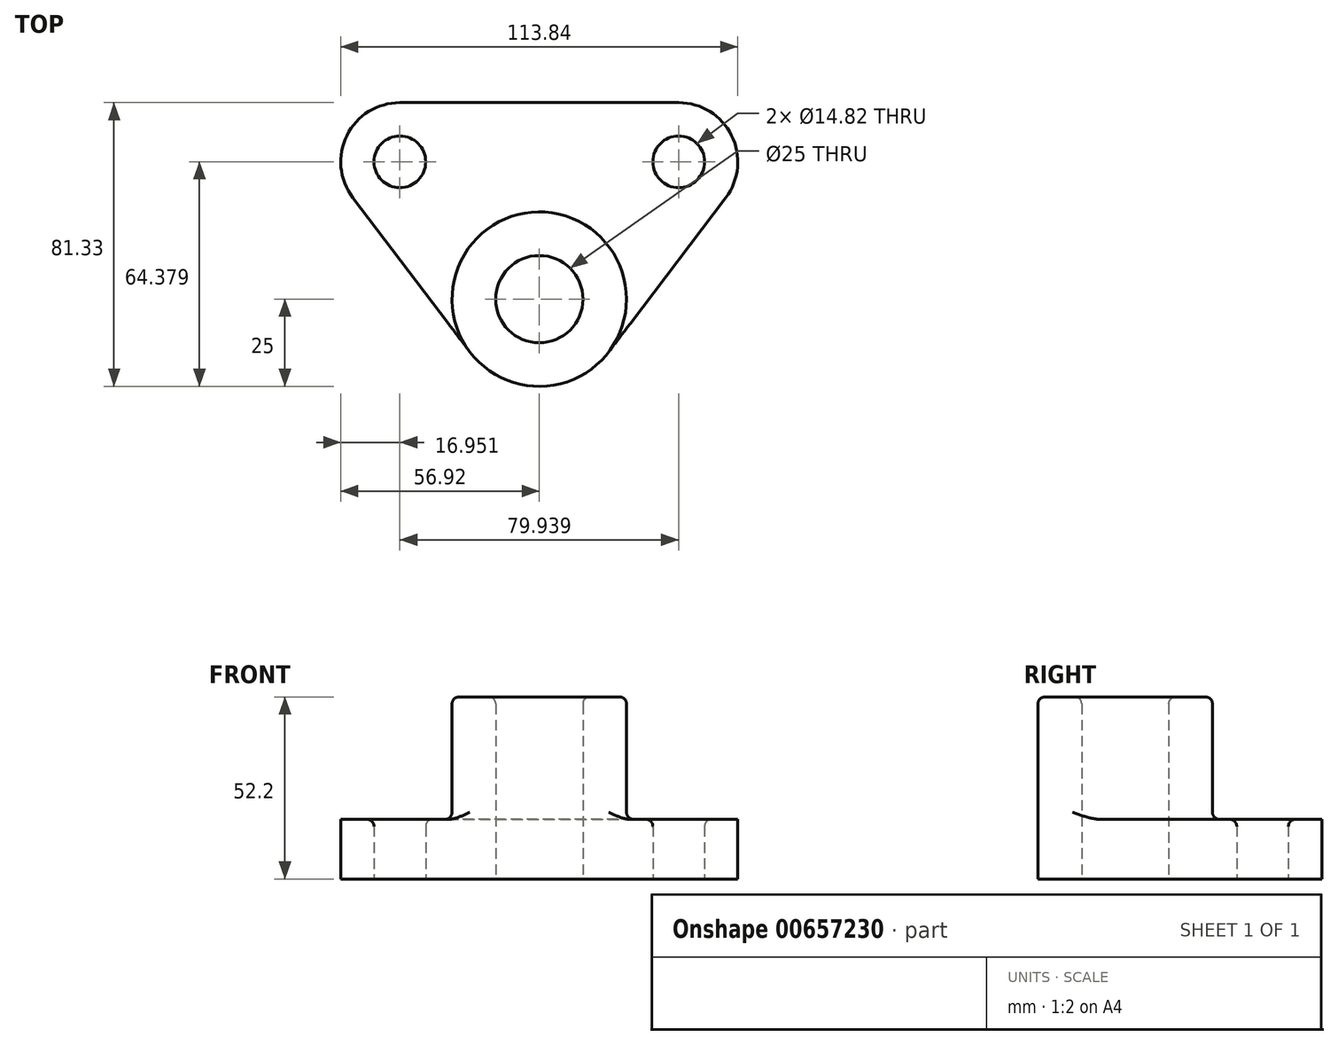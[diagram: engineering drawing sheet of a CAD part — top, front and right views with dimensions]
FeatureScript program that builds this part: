
annotation { "Feature Type Name" : "Feature", "Feature Type Description" : "" }
export const myFeature = defineFeature(function(context is Context, id is Id, definition is map)
    precondition{}
    {
        {
            var Q0;
            Q0=qCreatedBy(makeId("Top.planeOp"),FACE);
            var sketch = newSketch(context, id + "F0", { "sketchPlane" : qUnion([Q0])});
            skCircle(sketch, "E0", {"center": v(0, 0) * mm, "radius": 25 * mm});
            skCircle(sketch, "E1", {"center": v(0, 0) * mm, "radius": 12.5 * mm});
            skCircle(sketch, "E2", {"center": v(39.97, 39.38) * mm, "radius": 16.96 * mm});
            skCircle(sketch, "E3", {"center": v(39.97, 39.38) * mm, "radius": 7.41 * mm});
            skLineSegment(sketch, "E4", {"start": v(53.48, 29.13) * mm, "end": v(19.92, -15.1) * mm});
            skCircle(sketch, "E5.MirrorC", {"center": v(-39.97, 39.38) * mm, "radius": 16.96 * mm});
            skCircle(sketch, "E6.MirrorC", {"center": v(-39.97, 39.38) * mm, "radius": 7.41 * mm});
            skLineSegment(sketch, "E7.MirrorCS", {"start": v(-53.48, 29.13) * mm, "end": v(-19.92, -15.1) * mm});
            skPoint(sketch, "E8.orphan", {"position": v(-14.81, 20.14) * mm});
            skPoint(sketch, "E9.orphan", {"position": v(14.81, 20.14) * mm});
            skLineSegment(sketch, "E10", {"start": v(-39.97, 56.33) * mm, "end": v(39.97, 56.33) * mm});
            skSolve(sketch);
        }
        {
            var Q0;
            Q0 = qSketchRegion(id + "F0", true);
            extrude(context, id + "F1", {"entities" : qUnion([Q0]), "depth" : 17.1 * mm, "offsetDistance" : 25 * mm});
        }
        {
            var Q0;
            Q0=makeQuery(id+"F0.imprint","IMPRINT",FACE,{"disambiguationData":[TD([[makeQuery(id+"F0.imprint","IMPRINT",EDGE,{"derivedFrom":sQuery(id+"F0.wireOp",EDGE,"E1")}),-1.0]])]});
            extrude(context, id + "F2", {"entities" : qUnion([Q0]), "operationType" : NewBodyOperationType.ADD, "depth" : 52.2 * mm, "offsetDistance" : 25 * mm});
        }
        {
            var Q0;
            {var subQ0=sQuery(id+"F0.wireOp",EDGE,"E0");Q0=makeQuery(id+"F2.boolean.opBoolean","INTERSECT",EDGE,{"derivedFrom":[makeQuery(id+"F1.opExtrude","CAP_FACE",FACE,{"disambiguationData":[OSD([subQ0,sQuery(id+"F0.wireOp",EDGE,"E1"),sQuery(id+"F0.wireOp",EDGE,"E2"),sQuery(id+"F0.wireOp",EDGE,"E3"),sQuery(id+"F0.wireOp",EDGE,"E4"),sQuery(id+"F0.wireOp",EDGE,"E5.MirrorC"),sQuery(id+"F0.wireOp",EDGE,"E6.MirrorC"),sQuery(id+"F0.wireOp",EDGE,"E7.MirrorCS"),sQuery(id+"F0.wireOp",EDGE,"E10")])],"isStart":false}),makeQuery(id+"F2.opExtrude","SWEPT_FACE",FACE,{"disambiguationData":[OSD([subQ0])]})]});}
            fillet(context, id + "F3", {"entities" : qUnion([Q0]), "radius" : 2 * mm, "tangentPropagation" : true, "allowEdgeOverflow" : false});
        }
        {
            var Q0;
            Q0=makeQuery(id+"F2.opExtrude","CAP_EDGE",EDGE,{"disambiguationData":[OSD([sQuery(id+"F0.wireOp",EDGE,"E0")])],"isStart":false});
            var Q1;
            Q1=makeQuery(id+"F2.opExtrude","CAP_EDGE",EDGE,{"disambiguationData":[OSD([sQuery(id+"F0.wireOp",EDGE,"E1")])],"isStart":false});
            var Q2;
            Q2=makeQuery(id+"F1.opExtrude","CAP_EDGE",EDGE,{"disambiguationData":[OSD([sQuery(id+"F0.wireOp",EDGE,"E3")])],"isStart":false});
            var Q3;
            Q3=makeQuery(id+"F1.opExtrude","CAP_EDGE",EDGE,{"disambiguationData":[OSD([sQuery(id+"F0.wireOp",EDGE,"E6.MirrorC")])],"isStart":false});
            fillet(context, id + "F4", {"entities" : qUnion([Q0, Q1, Q2, Q3]), "radius" : 2 * mm, "tangentPropagation" : true, "allowEdgeOverflow" : false});
        }
    });
